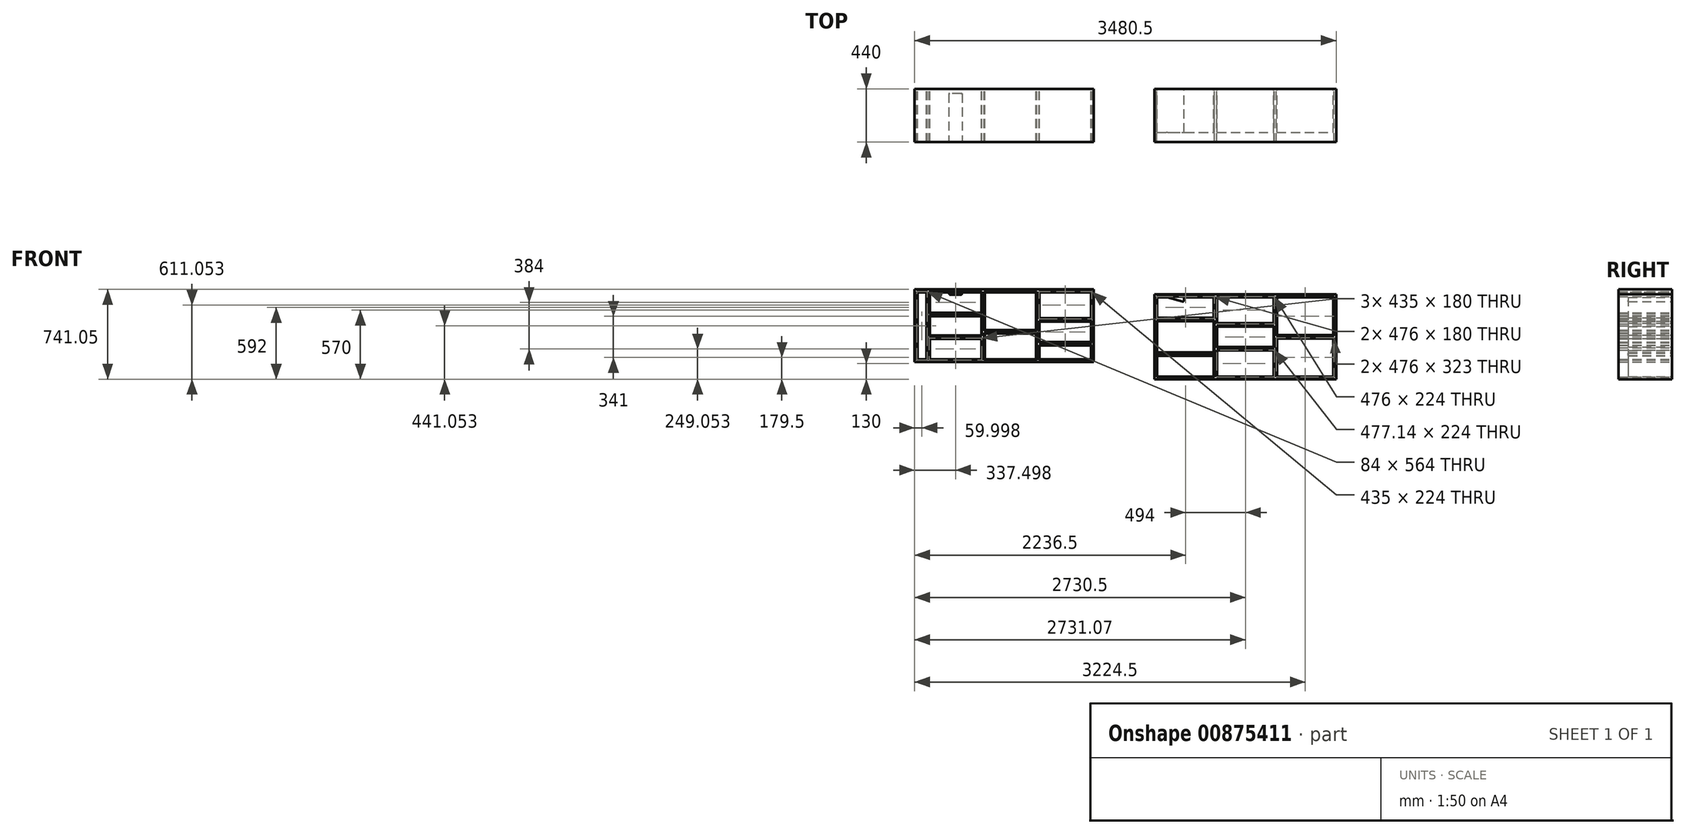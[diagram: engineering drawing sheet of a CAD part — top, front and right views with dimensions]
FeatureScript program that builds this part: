
annotation { "Feature Type Name" : "Feature", "Feature Type Description" : "" }
export const myFeature = defineFeature(function(context is Context, id is Id, definition is map)
    precondition{}
    {
        {
            var Q0;
            Q0=qCreatedBy(makeId("Front.planeOp"),FACE);
            var sketch = newSketch(context, id + "F0", { "sketchPlane" : qUnion([Q0])});
            skLineSegment(sketch, "E0.bottom", {"start": v(0, 0) * mm, "end": v(1500, 0) * mm});
            skLineSegment(sketch, "E0.top", {"start": v(0, -700) * mm, "end": v(1500, -700) * mm});
            skLineSegment(sketch, "E0.left", {"start": v(0, 0) * mm, "end": v(0, -700) * mm});
            skLineSegment(sketch, "E0.right", {"start": v(1500, 0) * mm, "end": v(1500, -700) * mm});
            skLineSegment(sketch, "E1.0", {"start": v(18, -18) * mm, "end": v(494, -18) * mm});
            skLineSegment(sketch, "E2.0", {"start": v(18, -18) * mm, "end": v(18, -198) * mm});
            skLineSegment(sketch, "E3.0", {"start": v(1482, -18) * mm, "end": v(1482, -341) * mm});
            skLineSegment(sketch, "E4.0", {"start": v(18, -682) * mm, "end": v(494, -682) * mm});
            skLineSegment(sketch, "E5.0", {"start": v(494, -18) * mm, "end": v(494, -198) * mm});
            skLineSegment(sketch, "E6.0", {"start": v(512, -18) * mm, "end": v(512, -242) * mm});
            skLineSegment(sketch, "E7.0", {"start": v(988, -18) * mm, "end": v(988, -242) * mm});
            skLineSegment(sketch, "E8.0", {"start": v(1006, -18) * mm, "end": v(1006, -341) * mm});
            skLineSegment(sketch, "E9.trimOffspring", {"start": v(1006, -18) * mm, "end": v(1482, -18) * mm});
            skLineSegment(sketch, "E10.trimOffspring", {"start": v(1006, -682) * mm, "end": v(1482, -682) * mm});
            skLineSegment(sketch, "E11.trimOffspring", {"start": v(512, -682) * mm, "end": v(989.14, -682) * mm});
            skLineSegment(sketch, "E12.trimOffspring", {"start": v(512, -18) * mm, "end": v(988, -18) * mm});
            skPoint(sketch, "E13", {"position": v(18, -198) * mm});
            skLineSegment(sketch, "E14", {"start": v(18, -198) * mm, "end": v(494, -198) * mm});
            skLineSegment(sketch, "E15.0", {"start": v(18, -216) * mm, "end": v(494, -216) * mm});
            skLineSegment(sketch, "E16.trimOffspring", {"start": v(494, -216) * mm, "end": v(494, -484) * mm});
            skLineSegment(sketch, "E17.trimOffspring", {"start": v(988, -206) * mm, "end": v(988, -260) * mm});
            skLineSegment(sketch, "E18.trimOffspring", {"start": v(1006, -359) * mm, "end": v(1006, -682) * mm});
            skLineSegment(sketch, "E19.trimOffspring", {"start": v(1482, -359) * mm, "end": v(1482, -682) * mm});
            skLineSegment(sketch, "E20.trimOffspring", {"start": v(18, -216) * mm, "end": v(18, -484) * mm});
            skLineSegment(sketch, "E21.0", {"start": v(23, -23) * mm, "end": v(23, -193) * mm});
            skLineSegment(sketch, "E21.1", {"start": v(23, -23) * mm, "end": v(489, -23) * mm});
            skLineSegment(sketch, "E21.2", {"start": v(489, -23) * mm, "end": v(489, -193) * mm});
            skLineSegment(sketch, "E21.3", {"start": v(23, -193) * mm, "end": v(489, -193) * mm});
            skLineSegment(sketch, "E22.0", {"start": v(517, -23) * mm, "end": v(517, -237) * mm});
            skLineSegment(sketch, "E22.1", {"start": v(517, -23) * mm, "end": v(983, -23) * mm});
            skLineSegment(sketch, "E22.2", {"start": v(983, -23) * mm, "end": v(983, -237) * mm});
            skLineSegment(sketch, "E23.0", {"start": v(1011, -23) * mm, "end": v(1011, -336) * mm});
            skLineSegment(sketch, "E23.1", {"start": v(1011, -23) * mm, "end": v(1477, -23) * mm});
            skLineSegment(sketch, "E23.2", {"start": v(1477, -23) * mm, "end": v(1477, -336) * mm});
            skLineSegment(sketch, "E24.0", {"start": v(1011, -364) * mm, "end": v(1011, -677) * mm});
            skLineSegment(sketch, "E24.2", {"start": v(1477, -364) * mm, "end": v(1477, -677) * mm});
            skLineSegment(sketch, "E24.3", {"start": v(1011, -677) * mm, "end": v(1477, -677) * mm});
            skPoint(sketch, "E25", {"position": v(18, -502) * mm});
            skLineSegment(sketch, "E26", {"start": v(18, -502) * mm, "end": v(494, -502) * mm});
            skLineSegment(sketch, "E27", {"start": v(18, -502) * mm, "end": v(18, -682) * mm});
            skLineSegment(sketch, "E28", {"start": v(494, -502) * mm, "end": v(494, -502) * mm});
            skLineSegment(sketch, "E29", {"start": v(494, -502) * mm, "end": v(494, -682) * mm});
            skLineSegment(sketch, "E30.0", {"start": v(18, -484) * mm, "end": v(18, -484) * mm});
            skLineSegment(sketch, "E31", {"start": v(512, -178) * mm, "end": v(512, -242) * mm});
            skLineSegment(sketch, "E32", {"start": v(512, -260) * mm, "end": v(512, -440) * mm});
            skLineSegment(sketch, "E33", {"start": v(512, -242) * mm, "end": v(988, -242) * mm});
            skLineSegment(sketch, "E34", {"start": v(512, -260) * mm, "end": v(988, -260) * mm});
            skLineSegment(sketch, "E35", {"start": v(517, -237) * mm, "end": v(983, -237) * mm});
            skLineSegment(sketch, "E36", {"start": v(1006, -341) * mm, "end": v(1482, -341) * mm});
            skLineSegment(sketch, "E37", {"start": v(1006, -359) * mm, "end": v(1482, -359) * mm});
            skLineSegment(sketch, "E38", {"start": v(1011, -336) * mm, "end": v(1477, -336) * mm});
            skLineSegment(sketch, "E39", {"start": v(1011, -364) * mm, "end": v(1477, -364) * mm});
            skLineSegment(sketch, "E40.right", {"start": v(243.26, -28) * mm, "end": v(243.26, -48) * mm});
            skArc(sketch, "E41.filletArc", {"start": v(233.93, -57.98) * mm, "mid": v(240.57, -54.83) * mm, "end": v(243.26, -48) * mm});
            skLineSegment(sketch, "E42", {"start": v(108.37, -24.38) * mm, "end": v(232.75, -57.86) * mm});
            skPoint(sketch, "E43.visualSharp", {"position": v(233.26, -58) * mm});
            skArc(sketch, "E43.filletArc", {"start": v(232.75, -57.86) * mm, "mid": v(233.34, -57.97) * mm, "end": v(233.93, -57.98) * mm});
            skPoint(sketch, "E44.visualSharp", {"position": v(103.26, -23) * mm});
            skArc(sketch, "E44.filletArc", {"start": v(108.37, -24.38) * mm, "mid": v(103.22, -23.35) * mm, "end": v(97.97, -23) * mm});
            skLineSegment(sketch, "E45", {"start": v(248.26, -23) * mm, "end": v(258.26, -23) * mm});
            skArc(sketch, "E46.filletArc", {"start": v(248.26, -23) * mm, "mid": v(244.73, -24.46) * mm, "end": v(243.26, -28) * mm});
            skLineSegment(sketch, "E47", {"start": v(18, -484) * mm, "end": v(18, -502) * mm});
            skLineSegment(sketch, "E48", {"start": v(18, -484) * mm, "end": v(494, -484) * mm});
            skLineSegment(sketch, "E49", {"start": v(494, -484) * mm, "end": v(494, -502) * mm});
            skLineSegment(sketch, "E50.0", {"start": v(23, -221) * mm, "end": v(489, -221) * mm});
            skLineSegment(sketch, "E50.1", {"start": v(23, -221) * mm, "end": v(23, -479) * mm});
            skLineSegment(sketch, "E50.2", {"start": v(23, -479) * mm, "end": v(489, -479) * mm});
            skLineSegment(sketch, "E50.3", {"start": v(489, -221) * mm, "end": v(489, -479) * mm});
            skLineSegment(sketch, "E51.0", {"start": v(23, -507) * mm, "end": v(23, -677) * mm});
            skLineSegment(sketch, "E51.1", {"start": v(23, -507) * mm, "end": v(489, -507) * mm});
            skLineSegment(sketch, "E51.2", {"start": v(489, -507) * mm, "end": v(489, -677) * mm});
            skLineSegment(sketch, "E51.3", {"start": v(23, -677) * mm, "end": v(489, -677) * mm});
            skPoint(sketch, "E52", {"position": v(512, -440) * mm});
            skLineSegment(sketch, "E53", {"start": v(512, -440) * mm, "end": v(988, -440) * mm});
            skLineSegment(sketch, "E54.0", {"start": v(512, -458) * mm, "end": v(989.14, -458) * mm});
            skLineSegment(sketch, "E55", {"start": v(988, -458) * mm, "end": v(988, -458) * mm});
            skLineSegment(sketch, "E56", {"start": v(989.14, -458) * mm, "end": v(989.14, -682) * mm});
            skLineSegment(sketch, "E57", {"start": v(512, -458) * mm, "end": v(512, -682) * mm});
            skLineSegment(sketch, "E58.0", {"start": v(517, -463) * mm, "end": v(984.14, -463) * mm});
            skLineSegment(sketch, "E58.1", {"start": v(517, -463) * mm, "end": v(517, -677) * mm});
            skLineSegment(sketch, "E58.2", {"start": v(517, -677) * mm, "end": v(984.14, -677) * mm});
            skLineSegment(sketch, "E58.3", {"start": v(984.14, -463) * mm, "end": v(984.14, -677) * mm});
            skLineSegment(sketch, "E59", {"start": v(988, -260) * mm, "end": v(988, -440) * mm});
            skLineSegment(sketch, "E60.0", {"start": v(517, -265) * mm, "end": v(983, -265) * mm});
            skLineSegment(sketch, "E60.1", {"start": v(517, -265) * mm, "end": v(517, -435) * mm});
            skLineSegment(sketch, "E60.2", {"start": v(517, -435) * mm, "end": v(983, -435) * mm});
            skLineSegment(sketch, "E60.3", {"start": v(983, -265) * mm, "end": v(983, -435) * mm});
            skLineSegment(sketch, "E61.bottom", {"start": v(-1980.5, 41.05) * mm, "end": v(-501.5, 41.05) * mm});
            skLineSegment(sketch, "E61.top", {"start": v(-1980.5, -558.95) * mm, "end": v(-501.5, -558.95) * mm});
            skLineSegment(sketch, "E61.left", {"start": v(-1980.5, 41.05) * mm, "end": v(-1980.5, -558.95) * mm});
            skLineSegment(sketch, "E61.right", {"start": v(-501.5, 41.05) * mm, "end": v(-501.5, -558.95) * mm});
            skLineSegment(sketch, "E62.0", {"start": v(-1980.5, 23.05) * mm, "end": v(-1425.5, 23.05) * mm});
            skLineSegment(sketch, "E63.0", {"start": v(-1860.5, 23.05) * mm, "end": v(-1860.5, -156.95) * mm});
            skLineSegment(sketch, "E64.0", {"start": v(-519.5, 23.05) * mm, "end": v(-519.5, -200.95) * mm});
            skLineSegment(sketch, "E65.0", {"start": v(-1860.5, -540.95) * mm, "end": v(-1425.5, -540.95) * mm});
            skLineSegment(sketch, "E66.0", {"start": v(-1425.5, 23.05) * mm, "end": v(-1425.5, -156.95) * mm});
            skLineSegment(sketch, "E67.0", {"start": v(-1407.5, 23.05) * mm, "end": v(-1407.5, -299.95) * mm});
            skLineSegment(sketch, "E68.0", {"start": v(-972.5, 23.05) * mm, "end": v(-972.5, -299.95) * mm});
            skLineSegment(sketch, "E69.0", {"start": v(-954.5, 23.05) * mm, "end": v(-954.5, -200.95) * mm});
            skLineSegment(sketch, "E70.trimOffspring", {"start": v(-954.5, 23.05) * mm, "end": v(-501.5, 23.05) * mm});
            skLineSegment(sketch, "E71.trimOffspring", {"start": v(-954.5, -540.95) * mm, "end": v(-519.5, -540.95) * mm});
            skLineSegment(sketch, "E72.trimOffspring", {"start": v(-1407.5, -540.95) * mm, "end": v(-972.5, -540.95) * mm});
            skLineSegment(sketch, "E73.trimOffspring", {"start": v(-1407.5, 23.05) * mm, "end": v(-972.5, 23.05) * mm});
            skPoint(sketch, "E74", {"position": v(-1860.5, -156.95) * mm});
            skLineSegment(sketch, "E75", {"start": v(-1860.5, -156.95) * mm, "end": v(-1425.5, -156.95) * mm});
            skLineSegment(sketch, "E76.0", {"start": v(-1860.5, -174.95) * mm, "end": v(-1425.5, -174.95) * mm});
            skLineSegment(sketch, "E77.trimOffspring", {"start": v(-1425.5, -174.95) * mm, "end": v(-1425.5, -342.95) * mm});
            skLineSegment(sketch, "E78.trimOffspring", {"start": v(-972.5, -64.95) * mm, "end": v(-972.5, -316.53) * mm});
            skLineSegment(sketch, "E79.trimOffspring", {"start": v(-954.5, -218.95) * mm, "end": v(-954.5, -398.95) * mm});
            skLineSegment(sketch, "E80.trimOffspring", {"start": v(-519.5, -218.95) * mm, "end": v(-519.5, -398.95) * mm});
            skLineSegment(sketch, "E81.trimOffspring", {"start": v(-1860.5, -174.95) * mm, "end": v(-1860.5, -342.95) * mm});
            skLineSegment(sketch, "E82.0", {"start": v(-1855.5, 18.05) * mm, "end": v(-1855.5, -151.95) * mm});
            skLineSegment(sketch, "E82.2", {"start": v(-1430.5, 18.05) * mm, "end": v(-1430.5, -151.95) * mm});
            skLineSegment(sketch, "E82.3", {"start": v(-1855.5, -151.95) * mm, "end": v(-1430.5, -151.95) * mm});
            skLineSegment(sketch, "E83.0", {"start": v(-1402.5, 18.05) * mm, "end": v(-1402.5, -294.95) * mm});
            skLineSegment(sketch, "E83.1", {"start": v(-1402.5, 18.05) * mm, "end": v(-977.5, 18.05) * mm});
            skLineSegment(sketch, "E83.2", {"start": v(-977.5, 18.05) * mm, "end": v(-977.5, -294.95) * mm});
            skLineSegment(sketch, "E84.0", {"start": v(-949.5, 18.05) * mm, "end": v(-949.5, -195.95) * mm});
            skLineSegment(sketch, "E84.1", {"start": v(-949.5, 18.05) * mm, "end": v(-524.5, 18.05) * mm});
            skLineSegment(sketch, "E84.2", {"start": v(-524.5, 18.05) * mm, "end": v(-524.5, -195.95) * mm});
            skLineSegment(sketch, "E85.0", {"start": v(-949.5, -223.95) * mm, "end": v(-949.5, -393.95) * mm});
            skLineSegment(sketch, "E85.2", {"start": v(-524.5, -223.95) * mm, "end": v(-524.5, -393.95) * mm});
            skLineSegment(sketch, "E85.3", {"start": v(-949.5, -535.95) * mm, "end": v(-524.5, -535.95) * mm});
            skPoint(sketch, "E86", {"position": v(-1860.5, -360.95) * mm});
            skLineSegment(sketch, "E87", {"start": v(-1860.5, -360.95) * mm, "end": v(-1425.5, -360.95) * mm});
            skLineSegment(sketch, "E88", {"start": v(-1860.5, -360.95) * mm, "end": v(-1860.5, -540.95) * mm});
            skLineSegment(sketch, "E89", {"start": v(-1425.5, -360.95) * mm, "end": v(-1425.5, -540.95) * mm});
            skLineSegment(sketch, "E90", {"start": v(-1407.5, -36.95) * mm, "end": v(-1407.5, -299.95) * mm});
            skLineSegment(sketch, "E91", {"start": v(-1407.5, -316.53) * mm, "end": v(-1407.5, -515.95) * mm});
            skLineSegment(sketch, "E92", {"start": v(-1407.5, -299.95) * mm, "end": v(-972.5, -299.95) * mm});
            skLineSegment(sketch, "E93", {"start": v(-1407.5, -316.53) * mm, "end": v(-972.5, -316.53) * mm});
            skLineSegment(sketch, "E94", {"start": v(-1402.5, -294.95) * mm, "end": v(-977.5, -294.95) * mm});
            skLineSegment(sketch, "E95", {"start": v(-954.5, -200.95) * mm, "end": v(-519.5, -200.95) * mm});
            skLineSegment(sketch, "E96", {"start": v(-954.5, -218.95) * mm, "end": v(-519.5, -218.95) * mm});
            skLineSegment(sketch, "E97", {"start": v(-949.5, -195.95) * mm, "end": v(-524.5, -195.95) * mm});
            skLineSegment(sketch, "E98", {"start": v(-949.5, -223.95) * mm, "end": v(-524.5, -223.95) * mm});
            skLineSegment(sketch, "E99", {"start": v(-920.02, -437.68) * mm, "end": v(-920.02, -437.68) * mm});
            skLineSegment(sketch, "E100", {"start": v(-1860.5, -342.95) * mm, "end": v(-1425.5, -342.95) * mm});
            skLineSegment(sketch, "E101.0", {"start": v(-1855.5, -179.95) * mm, "end": v(-1430.5, -179.95) * mm});
            skLineSegment(sketch, "E101.1", {"start": v(-1855.5, -179.95) * mm, "end": v(-1855.5, -337.95) * mm});
            skLineSegment(sketch, "E101.2", {"start": v(-1855.5, -337.95) * mm, "end": v(-1430.5, -337.95) * mm});
            skLineSegment(sketch, "E101.3", {"start": v(-1430.5, -179.95) * mm, "end": v(-1430.5, -337.95) * mm});
            skLineSegment(sketch, "E102.0", {"start": v(-1855.5, -365.95) * mm, "end": v(-1855.5, -535.95) * mm});
            skLineSegment(sketch, "E102.1", {"start": v(-1855.5, -365.95) * mm, "end": v(-1430.5, -365.95) * mm});
            skLineSegment(sketch, "E102.2", {"start": v(-1430.5, -365.95) * mm, "end": v(-1430.5, -535.95) * mm});
            skLineSegment(sketch, "E102.3", {"start": v(-1855.5, -535.95) * mm, "end": v(-1430.5, -535.95) * mm});
            skPoint(sketch, "E103", {"position": v(-1407.5, -497.95) * mm});
            skLineSegment(sketch, "E104", {"start": v(49.98, -411.68) * mm, "end": v(49.98, -411.68) * mm});
            skLineSegment(sketch, "E105", {"start": v(-1407.5, -515.95) * mm, "end": v(-1407.5, -540.95) * mm});
            skLineSegment(sketch, "E106.1", {"start": v(-1402.5, -321.53) * mm, "end": v(-1402.5, -535.95) * mm});
            skLineSegment(sketch, "E106.2", {"start": v(-1402.5, -535.95) * mm, "end": v(-977.5, -535.95) * mm});
            skLineSegment(sketch, "E107", {"start": v(-972.5, -316.53) * mm, "end": v(-972.5, -540.95) * mm});
            skLineSegment(sketch, "E108.0", {"start": v(-1402.5, -321.53) * mm, "end": v(-977.5, -321.53) * mm});
            skPoint(sketch, "E109", {"position": v(-954.5, -398.95) * mm});
            skLineSegment(sketch, "E110", {"start": v(-954.5, -398.95) * mm, "end": v(-519.5, -398.95) * mm});
            skLineSegment(sketch, "E111.0", {"start": v(-954.5, -416.95) * mm, "end": v(-519.5, -416.95) * mm});
            skLineSegment(sketch, "E112.0", {"start": v(-949.5, -393.95) * mm, "end": v(-524.5, -393.95) * mm});
            skLineSegment(sketch, "E113.0", {"start": v(-949.5, -421.95) * mm, "end": v(-524.5, -421.95) * mm});
            skLineSegment(sketch, "E114.trimOffspring", {"start": v(-949.5, -421.95) * mm, "end": v(-949.5, -535.95) * mm});
            skLineSegment(sketch, "E115.trimOffspring", {"start": v(-524.5, -421.95) * mm, "end": v(-524.5, -535.95) * mm});
            skLineSegment(sketch, "E116.trimOffspring", {"start": v(-954.5, -416.95) * mm, "end": v(-954.5, -540.95) * mm});
            skLineSegment(sketch, "E117.trimOffspring", {"start": v(-519.5, -416.95) * mm, "end": v(-519.5, -540.95) * mm});
            skLineSegment(sketch, "E118.0", {"start": v(-977.5, -321.53) * mm, "end": v(-977.5, -535.95) * mm});
            skLineSegment(sketch, "E119", {"start": v(-1430.5, 18.05) * mm, "end": v(-1855.5, 18.05) * mm});
            skLineSegment(sketch, "E120.bottom", {"start": v(-1962.5, 23.05) * mm, "end": v(-1878.5, 23.05) * mm});
            skLineSegment(sketch, "E120.top", {"start": v(-1962.5, -540.95) * mm, "end": v(-1878.5, -540.95) * mm});
            skLineSegment(sketch, "E120.left", {"start": v(-1962.5, 23.05) * mm, "end": v(-1962.5, -540.95) * mm});
            skLineSegment(sketch, "E120.right", {"start": v(-1878.5, 23.05) * mm, "end": v(-1878.5, -540.95) * mm});
            skLineSegment(sketch, "E121.0", {"start": v(-1957.5, 18.05) * mm, "end": v(-1957.5, -535.95) * mm});
            skLineSegment(sketch, "E121.1", {"start": v(-1957.5, 18.05) * mm, "end": v(-1883.5, 18.05) * mm});
            skLineSegment(sketch, "E121.2", {"start": v(-1883.5, 18.05) * mm, "end": v(-1883.5, -535.95) * mm});
            skLineSegment(sketch, "E121.3", {"start": v(-1957.5, -535.95) * mm, "end": v(-1883.5, -535.95) * mm});
            skSolve(sketch);
        }
        {
            var Q0;
            Q0=makeQuery(id+"F0.imprint","IMPRINT",FACE,{"disambiguationData":[TD([[makeQuery(id+"F0.imprint","IMPRINT",EDGE,{"derivedFrom":sQuery(id+"F0.wireOp",EDGE,"E26")}),1.0]])]});
            var Q1;
            Q1=makeQuery(id+"F0.imprint","IMPRINT",FACE,{"disambiguationData":[TD([[makeQuery(id+"F0.imprint","IMPRINT",EDGE,{"derivedFrom":sQuery(id+"F0.wireOp",EDGE,"E0.bottom")}),-1.0]])]});
            extrude(context, id + "F1", {"entities" : qUnion([Q0, Q1]), "depth" : 360 * mm, "offsetDistance" : 25 * mm});
        }
        {
            var Q0;
            Q0=makeQuery(id+"F0.imprint","IMPRINT",FACE,{"disambiguationData":[TD([[makeQuery(id+"F0.imprint","IMPRINT",EDGE,{"derivedFrom":sQuery(id+"F0.wireOp",EDGE,"E21.0")}),1.0]])]});
            var Q1;
            Q1=makeQuery(id+"F0.imprint","IMPRINT",FACE,{"disambiguationData":[TD([[makeQuery(id+"F0.imprint","IMPRINT",EDGE,{"derivedFrom":sQuery(id+"F0.wireOp",EDGE,"E22.0")}),1.0]])]});
            var Q2;
            Q2=makeQuery(id+"F0.imprint","IMPRINT",FACE,{"disambiguationData":[TD([[makeQuery(id+"F0.imprint","IMPRINT",EDGE,{"derivedFrom":sQuery(id+"F0.wireOp",EDGE,"E23.0")}),1.0]])]});
            var Q3;
            Q3=makeQuery(id+"F0.imprint","IMPRINT",FACE,{"disambiguationData":[TD([[makeQuery(id+"F0.imprint","IMPRINT",EDGE,{"derivedFrom":sQuery(id+"F0.wireOp",EDGE,"E50.0")}),-1.0]])]});
            var Q4;
            Q4=makeQuery(id+"F0.imprint","IMPRINT",FACE,{"disambiguationData":[TD([[makeQuery(id+"F0.imprint","IMPRINT",EDGE,{"derivedFrom":sQuery(id+"F0.wireOp",EDGE,"E51.0")}),1.0]])]});
            var Q5;
            Q5=makeQuery(id+"F0.imprint","IMPRINT",FACE,{"disambiguationData":[TD([[makeQuery(id+"F0.imprint","IMPRINT",EDGE,{"derivedFrom":sQuery(id+"F0.wireOp",EDGE,"E24.0")}),1.0]])]});
            var Q6;
            Q6=makeQuery(id+"F0.imprint","IMPRINT",FACE,{"disambiguationData":[TD([[makeQuery(id+"F0.imprint","IMPRINT",EDGE,{"derivedFrom":sQuery(id+"F0.wireOp",EDGE,"E60.0")}),-1.0]])]});
            var Q7;
            Q7=makeQuery(id+"F0.imprint","IMPRINT",FACE,{"disambiguationData":[TD([[makeQuery(id+"F0.imprint","IMPRINT",EDGE,{"derivedFrom":sQuery(id+"F0.wireOp",EDGE,"E58.0")}),-1.0]])]});
            extrude(context, id + "F2", {"entities" : qUnion([Q0, Q1, Q2, Q3, Q4, Q5, Q6, Q7]), "depth" : 360 * mm, "offsetDistance" : 25 * mm});
        }
        {
            var Q0;
            Q0 = qSketchRegion(id + "F0", true);
            extrude(context, id + "F3", {"entities" : qUnion([Q0]), "operationType" : NewBodyOperationType.ADD, "depth" : 440 * mm, "offsetDistance" : 25 * mm});
        }
        {
            var Q0;
            Q0=makeQuery(id+"F0.imprint","IMPRINT",FACE,{"disambiguationData":[TD([[makeQuery(id+"F0.imprint","IMPRINT",EDGE,{"derivedFrom":sQuery(id+"F0.wireOp",EDGE,"E84.0")}),1.0]])]});
            var Q1;
            Q1=makeQuery(id+"F0.imprint","IMPRINT",FACE,{"disambiguationData":[TD([[makeQuery(id+"F0.imprint","IMPRINT",EDGE,{"derivedFrom":sQuery(id+"F0.wireOp",EDGE,"E85.0")}),1.0]])]});
            var Q2;
            Q2=makeQuery(id+"F0.imprint","IMPRINT",FACE,{"disambiguationData":[TD([[makeQuery(id+"F0.imprint","IMPRINT",EDGE,{"derivedFrom":sQuery(id+"F0.wireOp",EDGE,"E85.3")}),1.0]])]});
            var Q3;
            Q3=makeQuery(id+"F0.imprint","IMPRINT",FACE,{"disambiguationData":[TD([[makeQuery(id+"F0.imprint","IMPRINT",EDGE,{"derivedFrom":sQuery(id+"F0.wireOp",EDGE,"E83.0")}),1.0]])]});
            var Q4;
            Q4=makeQuery(id+"F0.imprint","IMPRINT",FACE,{"disambiguationData":[TD([[makeQuery(id+"F0.imprint","IMPRINT",EDGE,{"derivedFrom":sQuery(id+"F0.wireOp",EDGE,"E106.1")}),1.0]])]});
            var Q5;
            {var subQ2=sQuery(id+"F0.wireOp",EDGE,"E82.0");Q5=makeQuery(id+"F0.imprint","IMPRINT",FACE,{"disambiguationData":[TD([[makeQuery(id+"F0.imprint","IMPRINT",EDGE,{"derivedFrom":subQ2}),1.0]])]});}
            var Q6;
            Q6=makeQuery(id+"F0.imprint","IMPRINT",FACE,{"disambiguationData":[TD([[makeQuery(id+"F0.imprint","IMPRINT",EDGE,{"derivedFrom":sQuery(id+"F0.wireOp",EDGE,"E101.0")}),-1.0]])]});
            var Q7;
            Q7=makeQuery(id+"F0.imprint","IMPRINT",FACE,{"disambiguationData":[TD([[makeQuery(id+"F0.imprint","IMPRINT",EDGE,{"derivedFrom":sQuery(id+"F0.wireOp",EDGE,"E102.0")}),1.0]])]});
            var Q8;
            Q8=makeQuery(id+"F0.imprint","IMPRINT",FACE,{"disambiguationData":[TD([[makeQuery(id+"F0.imprint","IMPRINT",EDGE,{"derivedFrom":sQuery(id+"F0.wireOp",EDGE,"E121.0")}),1.0]])]});
            extrude(context, id + "F4", {"entities" : qUnion([Q0, Q1, Q2, Q3, Q4, Q5, Q6, Q7, Q8]), "operationType" : NewBodyOperationType.ADD, "depth" : 440 * mm, "offsetDistance" : 25 * mm});
        }
        {
            var Q0;
            Q0=makeQuery(id+"F4.opExtrude","CAP_FACE",FACE,{"disambiguationData":[OSD([sQuery(id+"F0.wireOp",EDGE,"E82.0"),sQuery(id+"F0.wireOp",EDGE,"E82.2"),sQuery(id+"F0.wireOp",EDGE,"E82.3"),sQuery(id+"F0.wireOp",EDGE,"E119")])],"isStart":false});
            var sketch = newSketch(context, id + "F5", { "sketchPlane" : qUnion([Q0])});
            skPoint(sketch, "E122", {"position": v(-1643, 18.05) * mm});
            skPoint(sketch, "E123", {"position": v(-1643, -1.95) * mm});
            skLineSegment(sketch, "E124", {"start": v(-1643, -1.95) * mm, "end": v(-1689.17, -1.95) * mm});
            skLineSegment(sketch, "E125", {"start": v(-1694, 1.76) * mm, "end": v(-1698.36, 18.05) * mm});
            skPoint(sketch, "E126.visualSharp", {"position": v(-1693, -1.95) * mm});
            skArc(sketch, "E126.filletArc", {"start": v(-1694, 1.76) * mm, "mid": v(-1692.2, -0.91) * mm, "end": v(-1689.17, -1.95) * mm});
            skLineSegment(sketch, "E127", {"start": v(-1643, 18.05) * mm, "end": v(-1643, -1.95) * mm, "construction": true});
            skLineSegment(sketch, "E128.MirrorCS", {"start": v(-1643, -1.95) * mm, "end": v(-1596.84, -1.95) * mm});
            skArc(sketch, "E129.MirrorCS", {"start": v(-1592, 1.76) * mm, "mid": v(-1593.8, -0.91) * mm, "end": v(-1596.84, -1.95) * mm});
            skLineSegment(sketch, "E130.MirrorCS", {"start": v(-1592, 1.76) * mm, "end": v(-1587.64, 18.05) * mm});
            skSolve(sketch);
        }
        {
            var Q0;
            Q0 = qSketchRegion(id + "F5", true);
            var Q1;
            Q1=makeQuery(id+"F5.imprint","IMPRINT",FACE,{"disambiguationData":[TD([[makeQuery(id+"F5.imprint","IMPRINT",EDGE,{"derivedFrom":sQuery(id+"F5.wireOp",EDGE,"E124")}),-1.0]])]});
            extrude(context, id + "F6", {"entities" : qUnion([Q0, Q1]), "operationType" : NewBodyOperationType.REMOVE, "oppositeDirection" : true, "depth" : 400 * mm, "offsetDistance" : 25 * mm});
        }
    });
